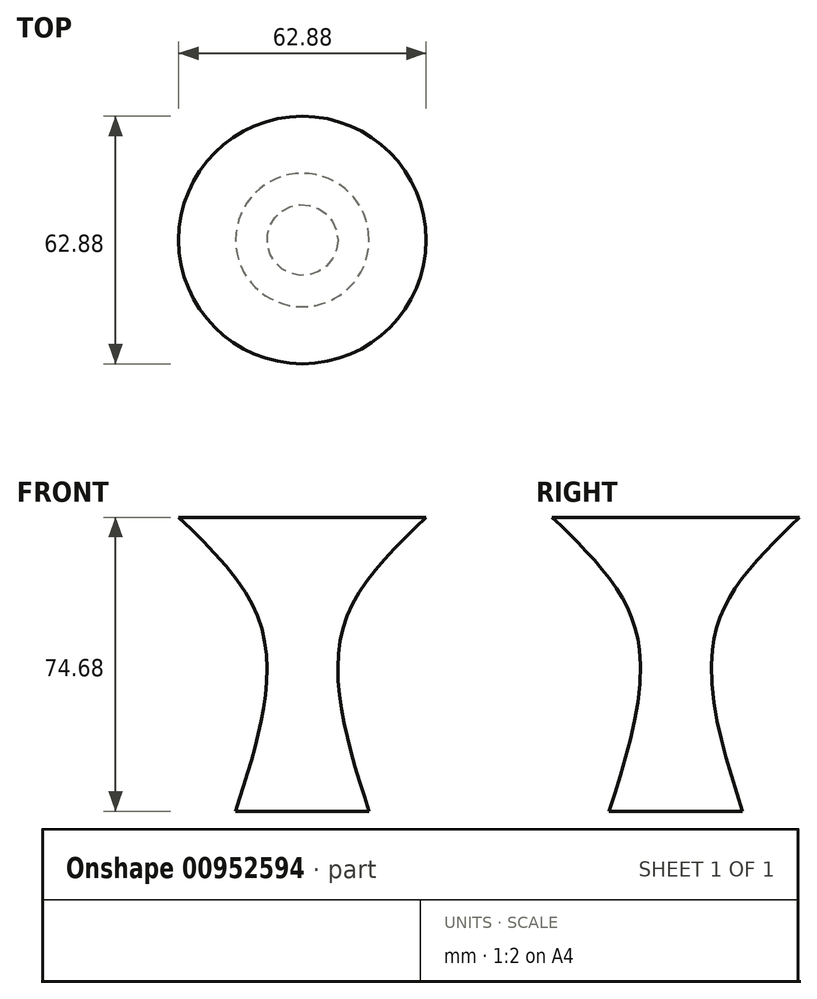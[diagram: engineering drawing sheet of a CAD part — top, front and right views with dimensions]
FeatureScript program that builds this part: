
annotation { "Feature Type Name" : "Feature", "Feature Type Description" : "" }
export const myFeature = defineFeature(function(context is Context, id is Id, definition is map)
    precondition{}
    {
        {
            var Q0;
            Q0=qCreatedBy(makeId("Top.planeOp"),FACE);
            var sketch = newSketch(context, id + "F0", { "sketchPlane" : qUnion([Q0])});
            skCircle(sketch, "E0", {"center": v(0, 0) * mm, "radius": 16.94 * mm});
            skSolve(sketch);
        }
        {
            var Q0;
            Q0=qCreatedBy(makeId("Top.planeOp"),FACE);
            cPlane(context, id + "F1", {"entities" : qUnion([Q0]), "cplaneType" : CPlaneType.OFFSET, "offset" : 49.28 * mm, "width" : 152.4 * mm, "height" : 152.4 * mm});
        }
        {
            var Q0;
            Q0=qCreatedBy(id+"F1.planeOp",FACE);
            var sketch = newSketch(context, id + "F2", { "sketchPlane" : qUnion([Q0])});
            skCircle(sketch, "E1", {"center": v(0, 0) * mm, "radius": 11.24 * mm});
            skSolve(sketch);
        }
        {
            var Q0;
            Q0=qCreatedBy(id+"F1.planeOp",FACE);
            cPlane(context, id + "F3", {"entities" : qUnion([Q0]), "cplaneType" : CPlaneType.OFFSET, "offset" : 25.4 * mm, "width" : 152.4 * mm, "height" : 152.4 * mm});
        }
        {
            var Q0;
            Q0=qCreatedBy(id+"F3.planeOp",FACE);
            var sketch = newSketch(context, id + "F4", { "sketchPlane" : qUnion([Q0])});
            skCircle(sketch, "E2", {"center": v(0, 0) * mm, "radius": 31.44 * mm});
            skSolve(sketch);
        }
        {
            var Q0;
            Q0=makeQuery(id+"F4.imprint","IMPRINT",FACE,{"disambiguationData":[TD([[makeQuery(id+"F4.imprint","IMPRINT",EDGE,{"derivedFrom":sQuery(id+"F4.wireOp",EDGE,"E2")}),1.0]])]});
            var Q1;
            Q1=makeQuery(id+"F2.imprint","IMPRINT",FACE,{"disambiguationData":[TD([[makeQuery(id+"F2.imprint","IMPRINT",EDGE,{"derivedFrom":sQuery(id+"F2.wireOp",EDGE,"E1")}),1.0]])]});
            var Q2;
            Q2=makeQuery(id+"F0.imprint","IMPRINT",FACE,{"disambiguationData":[TD([[makeQuery(id+"F0.imprint","IMPRINT",EDGE,{"derivedFrom":sQuery(id+"F0.wireOp",EDGE,"E0")}),1.0]])]});
            loft(context, id + "F5", {"sheetProfilesArray" : [{ "sheetProfileEntities" : qUnion([Q0]) }, { "sheetProfileEntities" : qUnion([Q1]) }, { "sheetProfileEntities" : qUnion([Q2]) }]});
        }
        {
            var Q0;
            Q0=qCreatedBy(id+"F3.planeOp",FACE);
            cPlane(context, id + "F6", {"entities" : qUnion([Q0]), "cplaneType" : CPlaneType.OFFSET, "offset" : 33.53 * mm, "width" : 152.4 * mm, "height" : 152.4 * mm});
        }
        {
            var Q0;
            Q0=qCreatedBy(id+"F6.planeOp",FACE);
            var sketch = newSketch(context, id + "F7", { "sketchPlane" : qUnion([Q0])});
            skCircle(sketch, "E3", {"center": v(0, 0) * mm, "radius": 26.06 * mm});
            skSolve(sketch);
        }
        {
            var Q0;
            Q0=sQuery(id+"F7.wireOp",EDGE,"E3");
            var Q1;
            Q1=makeQuery(id+"F5.opLoft","MID_CAP_EDGE",EDGE,{"disambiguationData":[OSD([sQuery(id+"F4.wireOp",EDGE,"E2")])],"capPos":0.0});
            loft(context, id + "F8", {"bodyType" : ToolBodyType.SURFACE, "wireProfilesArray" : [{ "wireProfileEntities" : qUnion([Q0]) }, { "wireProfileEntities" : qUnion([Q1]) }]});
        }
    });
